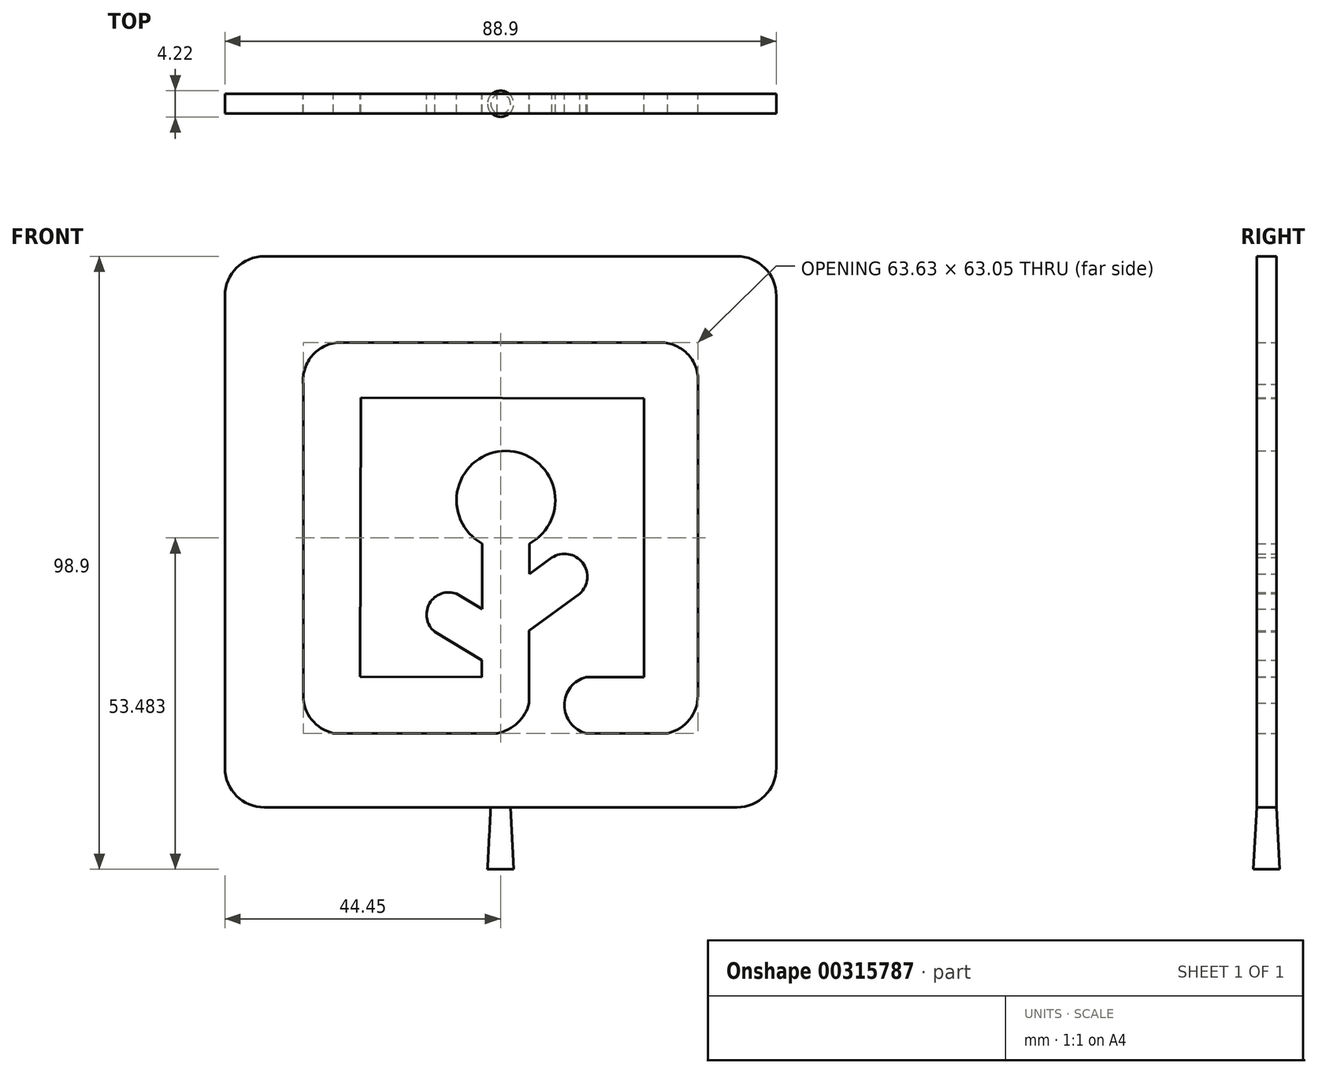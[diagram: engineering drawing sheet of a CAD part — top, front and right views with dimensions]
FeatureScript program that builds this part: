
annotation { "Feature Type Name" : "Feature", "Feature Type Description" : "" }
export const myFeature = defineFeature(function(context is Context, id is Id, definition is map)
    precondition{}
    {
        {
            var Q0;
            Q0=qCreatedBy(makeId("Front.planeOp"),FACE);
            var sketch = newSketch(context, id + "F0", { "sketchPlane" : qUnion([Q0])});
            skLineSegment(sketch, "E0", {"start": v(23.12, 15.16) * mm, "end": v(23.12, -29.78) * mm});
            skLineSegment(sketch, "E1", {"start": v(31.81, -32.76) * mm, "end": v(31.81, 17.48) * mm});
            skLineSegment(sketch, "E2", {"start": v(0, 43.38) * mm, "end": v(0, -69.91) * mm, "construction": true});
            skLineSegment(sketch, "E3", {"start": v(-73.66, 0) * mm, "end": v(31.81, 0) * mm, "construction": true});
            skPoint(sketch, "E4.visualSharp", {"position": v(-31.23, 23.83) * mm});
            skArc(sketch, "E5", {"start": v(26.96, -38.84) * mm, "mid": v(30.45, -36.65) * mm, "end": v(31.81, -32.76) * mm});
            skLineSegment(sketch, "E6", {"start": v(26.96, -38.84) * mm, "end": v(13.81, -38.84) * mm});
            skArc(sketch, "E7", {"start": v(13.81, -29.78) * mm, "mid": v(10.27, -34.31) * mm, "end": v(13.81, -38.84) * mm});
            skLineSegment(sketch, "E8", {"start": v(13.81, -29.78) * mm, "end": v(23.12, -29.78) * mm});
            skLineSegment(sketch, "E9", {"start": v(-22.54, 15.27) * mm, "end": v(23.12, 15.16) * mm});
            skLineSegment(sketch, "E10", {"start": v(-22.54, 15.27) * mm, "end": v(-22.65, -29.75) * mm});
            skLineSegment(sketch, "E11", {"start": v(-22.65, -29.75) * mm, "end": v(-3.02, -29.8) * mm});
            skLineSegment(sketch, "E12", {"start": v(-3.02, -29.8) * mm, "end": v(-3.02, -27.05) * mm});
            skLineSegment(sketch, "E13", {"start": v(-3.02, -27.05) * mm, "end": v(-10.6, -22.48) * mm});
            skArc(sketch, "E14", {"start": v(-7.07, -16.36) * mm, "mid": v(-11.46, -17.9) * mm, "end": v(-10.6, -22.48) * mm});
            skLineSegment(sketch, "E15", {"start": v(-7.07, -16.36) * mm, "end": v(-2.96, -18.8) * mm});
            skLineSegment(sketch, "E16", {"start": v(-2.96, -18.8) * mm, "end": v(-2.96, -8.26) * mm});
            skLineSegment(sketch, "E17", {"start": v(-2.96, -8.26) * mm, "end": v(4.66, -8.26) * mm, "construction": true});
            skLineSegment(sketch, "E18", {"start": v(4.66, -8.26) * mm, "end": v(4.66, -13.17) * mm});
            skLineSegment(sketch, "E19", {"start": v(4.66, -13.17) * mm, "end": v(8.27, -10.5) * mm});
            skArc(sketch, "E20", {"start": v(4.66, -8.26) * mm, "mid": v(0.85, 6.7) * mm, "end": v(-2.96, -8.26) * mm});
            skArc(sketch, "E21", {"start": v(12.75, -16.33) * mm, "mid": v(13.22, -11.34) * mm, "end": v(8.27, -10.5) * mm});
            skLineSegment(sketch, "E22", {"start": v(12.75, -16.33) * mm, "end": v(4.6, -22.29) * mm});
            skLineSegment(sketch, "E23", {"start": v(4.6, -22.29) * mm, "end": v(4.6, -33.96) * mm});
            skArc(sketch, "E24", {"start": v(-0.56, -38.84) * mm, "mid": v(2.75, -37.17) * mm, "end": v(4.6, -33.96) * mm});
            skLineSegment(sketch, "E25", {"start": v(-0.56, -38.84) * mm, "end": v(-26.96, -38.84) * mm});
            skLineSegment(sketch, "E26", {"start": v(0, 24.2) * mm, "end": v(25.76, 24.2) * mm});
            skArc(sketch, "E27", {"start": v(31.81, 17.48) * mm, "mid": v(30.28, 22.2) * mm, "end": v(25.76, 24.2) * mm});
            skLineSegment(sketch, "E28.MirrorCS", {"start": v(0, 24.2) * mm, "end": v(-25.76, 24.2) * mm});
            skArc(sketch, "E29.MirrorCS", {"start": v(-31.81, 17.48) * mm, "mid": v(-30.28, 22.2) * mm, "end": v(-25.76, 24.2) * mm});
            skLineSegment(sketch, "E30.MirrorCS", {"start": v(-31.81, -32.76) * mm, "end": v(-31.81, 17.48) * mm});
            skArc(sketch, "E31.MirrorCS", {"start": v(-26.96, -38.84) * mm, "mid": v(-30.45, -36.65) * mm, "end": v(-31.81, -32.76) * mm});
            skSolve(sketch);
        }
        {
            var Q0;
            Q0=qCreatedBy(makeId("Front.planeOp"),FACE);
            var sketch = newSketch(context, id + "F1", { "sketchPlane" : qUnion([Q0])});
            skLineSegment(sketch, "E32.bottom", {"start": v(-38.1, 38.1) * mm, "end": v(38.1, 38.1) * mm});
            skLineSegment(sketch, "E32.top", {"start": v(-38.1, -50.8) * mm, "end": v(38.1, -50.8) * mm});
            skLineSegment(sketch, "E32.left", {"start": v(-44.45, 31.75) * mm, "end": v(-44.45, -44.45) * mm});
            skLineSegment(sketch, "E32.right", {"start": v(44.45, 31.75) * mm, "end": v(44.45, -44.45) * mm});
            skPoint(sketch, "E33.visualSharp", {"position": v(-44.45, 38.1) * mm});
            skArc(sketch, "E33.filletArc", {"start": v(-38.1, 38.1) * mm, "mid": v(-42.6, 36.24) * mm, "end": v(-44.45, 31.75) * mm});
            skPoint(sketch, "E34.visualSharp", {"position": v(-44.45, -50.8) * mm});
            skArc(sketch, "E34.filletArc", {"start": v(-44.45, -44.45) * mm, "mid": v(-42.6, -48.94) * mm, "end": v(-38.1, -50.8) * mm});
            skPoint(sketch, "E35.visualSharp", {"position": v(44.45, -50.8) * mm});
            skArc(sketch, "E35.filletArc", {"start": v(38.1, -50.8) * mm, "mid": v(42.6, -48.94) * mm, "end": v(44.45, -44.45) * mm});
            skPoint(sketch, "E36.visualSharp", {"position": v(44.45, 38.1) * mm});
            skArc(sketch, "E36.filletArc", {"start": v(44.45, 31.75) * mm, "mid": v(42.6, 36.24) * mm, "end": v(38.1, 38.1) * mm});
            skSolve(sketch);
        }
        {
            var Q0;
            Q0 = qSketchRegion(id + "F1", true);
            extrude(context, id + "F2", {"entities" : qUnion([Q0]), "depth" : 3.17 * mm});
        }
        {
            var Q0;
            Q0 = qSketchRegion(id + "F0", true);
            extrude(context, id + "F3", {"entities" : qUnion([Q0]), "operationType" : NewBodyOperationType.REMOVE, "depth" : 6.35 * mm});
        }
        {
            var Q0;
            Q0=makeQuery(id+"F2.opExtrude","SWEPT_FACE",FACE,{"disambiguationData":[OSD([sQuery(id+"F1.wireOp",EDGE,"E32.top")])]});
            var sketch = newSketch(context, id + "F4", { "sketchPlane" : qUnion([Q0])});
            skCircle(sketch, "E37", {"center": v(0, 1.59) * mm, "radius": 1.59 * mm});
            skPoint(sketch, "E37.centerSnap0", {"position": v(0, 3.18) * mm});
            skLineSegment(sketch, "E38", {"start": v(0, 3.18) * mm, "end": v(0, 0) * mm, "construction": true});
            skSolve(sketch);
        }
        {
            var Q0;
            Q0 = qSketchRegion(id + "F4", true);
            extrude(context, id + "F5", {"entities" : qUnion([Q0]), "operationType" : NewBodyOperationType.ADD, "depth" : 10 * mm, "hasDraft" : true, "draftAngle" : 3 * degree});
        }
    });
